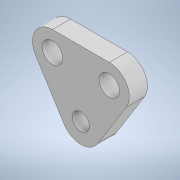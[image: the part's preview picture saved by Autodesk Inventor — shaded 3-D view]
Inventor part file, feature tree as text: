
AUTODESK INVENTOR PART (.ipt)
format: ipt  version: 2020 (Build 240168000, 168)  size: 118,272 bytes
history: native  units: mm
features: extrude x1, sketch x1
ambient origin geometry x8: Origin, YZ Plane, XZ Plane, XY Plane, X Axis, Y Axis, Z Axis, Center Point
bodies: Solid1 (feature_tree)
feature tree (2):
  extrude  "Extrusion1"  Depth=1.6mm
  sketch  "Sketch1"  dims[d0=5.0mm d1=3.5mm d2=4.0mm d3=1.8mm d4=1.6mm d5=0.0mm d6=1.5mm]
